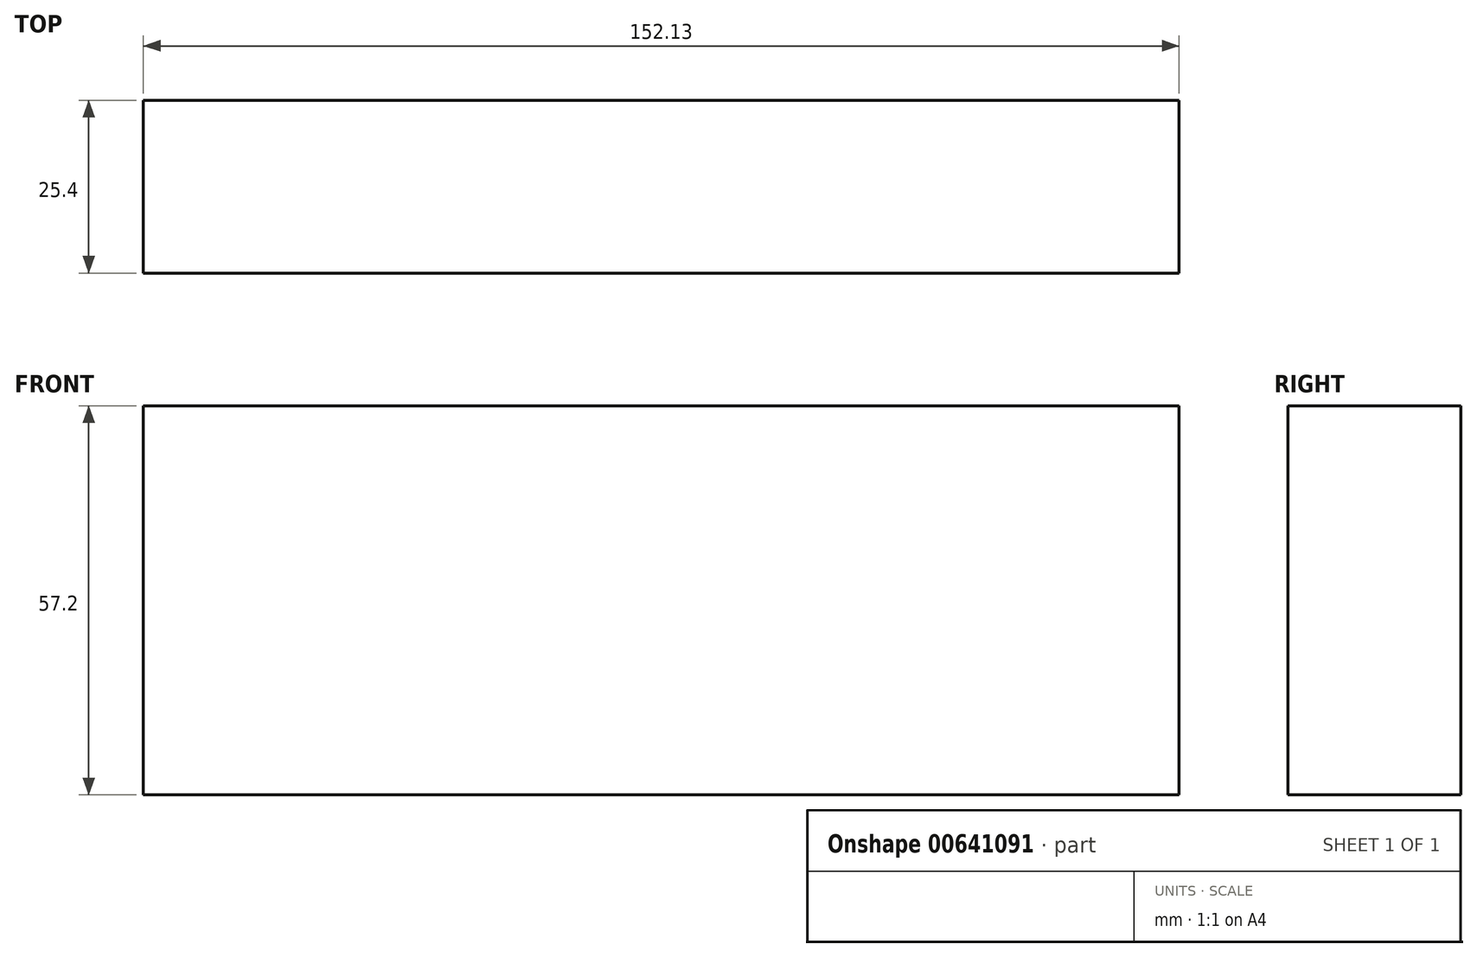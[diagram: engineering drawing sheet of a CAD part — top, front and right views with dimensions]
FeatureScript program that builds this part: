
annotation { "Feature Type Name" : "Feature", "Feature Type Description" : "" }
export const myFeature = defineFeature(function(context is Context, id is Id, definition is map)
    precondition{}
    {
        {
            var Q0;
            Q0=qCreatedBy(makeId("Front.planeOp"),FACE);
            var sketch = newSketch(context, id + "F0", { "sketchPlane" : qUnion([Q0])});
            skLineSegment(sketch, "E0.bottom", {"start": v(-76.32, 57.2) * mm, "end": v(75.8, 57.2) * mm});
            skLineSegment(sketch, "E0.top", {"start": v(-76.32, 0) * mm, "end": v(75.8, 0) * mm});
            skLineSegment(sketch, "E0.left", {"start": v(-76.32, 57.2) * mm, "end": v(-76.32, 0) * mm});
            skLineSegment(sketch, "E0.right", {"start": v(75.8, 57.2) * mm, "end": v(75.8, 0) * mm});
            skSolve(sketch);
        }
        {
            var Q0;
            Q0=makeQuery(id+"F0.imprint","IMPRINT",FACE,{"disambiguationData":[TD([[makeQuery(id+"F0.imprint","IMPRINT",EDGE,{"derivedFrom":sQuery(id+"F0.wireOp",EDGE,"E0.bottom")}),-1.0]])]});
            extrude(context, id + "F1", {"entities" : qUnion([Q0]), "depth" : 25.4 * mm, "offsetDistance" : 25.4 * mm});
        }
    });
